# Revit family: BuroSeating_Konfurb Star_Ottoman 1
name_source: partatom
category: Furniture
units: mm (PartAtom-declared; Revit-internal decimal feet)

## family parameters
Always vertical = Yes
Cut with Voids When Loaded = No
OmniClass Number = 23.40.70.14.64.11
OmniClass Title = Office Furniture
Room Calculation Point = No
Shared = No
Work Plane-Based = No

## types (1)
- KON723-OTT1
    Assembly Code = E2020
    BaseOffset = 18 mm  [stored 0.0590551 ft]
    Default Elevation = 0 mm  [stored 0 ft]
    Description = Konfub Star Ottoman 1
    FeetDiameter = 35 mm  [stored 0.114829 ft]
    FeetMaterial = BuroSeating_Plastic_Black
    Manufacturer = Buro Seating
    Model = KON723-OTT1
    NominalHeight = 450 mm  [stored 1.47638 ft]
    NominalLength = 816 mm
    NominalWidth = 858 mm
    ProductGroup = Star
    ProductPageURL AU = https://buroseating.com
    ProductPageURL NZ = https://buroseating.co.nz
    ProductRange = Konfurb
    SeatHeight = 450 mm  [stored 1.47638 ft]
    URL = https://buroseating.co.nz
    URL AU = https://buroseating.com
    WarrantyDescription = Full 5 year guarantee (excluding upholstery)

note: [stored X ft] marks values corroborated as IEEE doubles in the binary element streams (Revit-internal decimal feet)

## geometry (parser evidence)
native form markers: Sweep x5
no freeform markers — native parametric forms only
